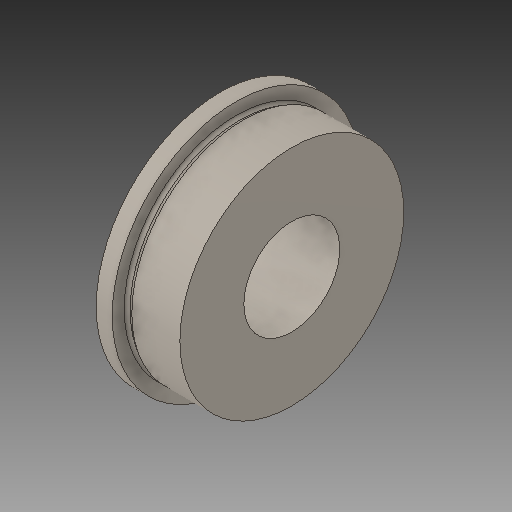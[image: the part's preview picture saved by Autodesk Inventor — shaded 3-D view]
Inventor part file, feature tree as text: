
AUTODESK INVENTOR PART (.ipt)
format: ipt  version: 2017 (Build 210142000, 142)  size: 151,040 bytes
history: native  units: in
note: dims shown in document units (in); Inventor stores cm internally (conversion verified against a paired STEP export)
features: revolve x1
ambient origin geometry x8: Origin, YZ Plane, XZ Plane, XY Plane, X Axis, Y Axis, Z Axis, Center Point
bodies: Solid1 (feature_tree)
feature tree (1):
  revolve  "Revolve1"  [1 undecoded]
note: 1 required parameter value undecoded (feature->parameter linkage not recoverable at this tier; creation-order binding heuristic only, values carry confidence <= 0.55)
